# Revit family: Furniture_Tables_Svedholm_Block
name_source: partatom
category: Furniture
revit_build: Autodesk Revit 2018 (Build: 20190510_1515(x64)
units: mm (PartAtom-declared; Revit-internal decimal feet)

## family parameters
Always vertical = Yes
Cut with Voids When Loaded = No
OmniClass Number = 23.21.23.00
OmniClass Title = Residential Furniture and Equipment
Room Calculation Point = No
Shared = No
Work Plane-Based = Yes

## types (1)
- ART - (208.600.001)
    BIMobject category = Tables
    Default Elevation = 1219 mm
    Description = A lounge table with table top of tempered glass. Table base of powder coated wire.
    Edition number = 1
    IFC Classification = Furniture
    Manufacturer = Svedholm
    Manufacturer name = Svedholm
    Model = Block
    OmniClass Code = 23-21 23 00
    OmniClass Description = Residential Furniture and Equipment
    Product Guid = ce8e9699-7a0f-4f5b-af11-03c5bdc37d56
    Product SKU = Block
    Product data url = https://bimobject.com
    Product family = Block
    Product group = Tables
    Product name = Block
    Product url = https://www.svedholm.se
    QR code = https://bimobject.com
    Tabletop material = Svedholm - Glass - Transparent
    UNSPSC Code = 56
    URL = https://www.svedholm.se
    Uniclass 1.4 Code = L8221
    Uniclass 1.4 Description = Tables

## geometry (parser evidence)
native form markers: Sweep x7
no freeform markers — native parametric forms only
